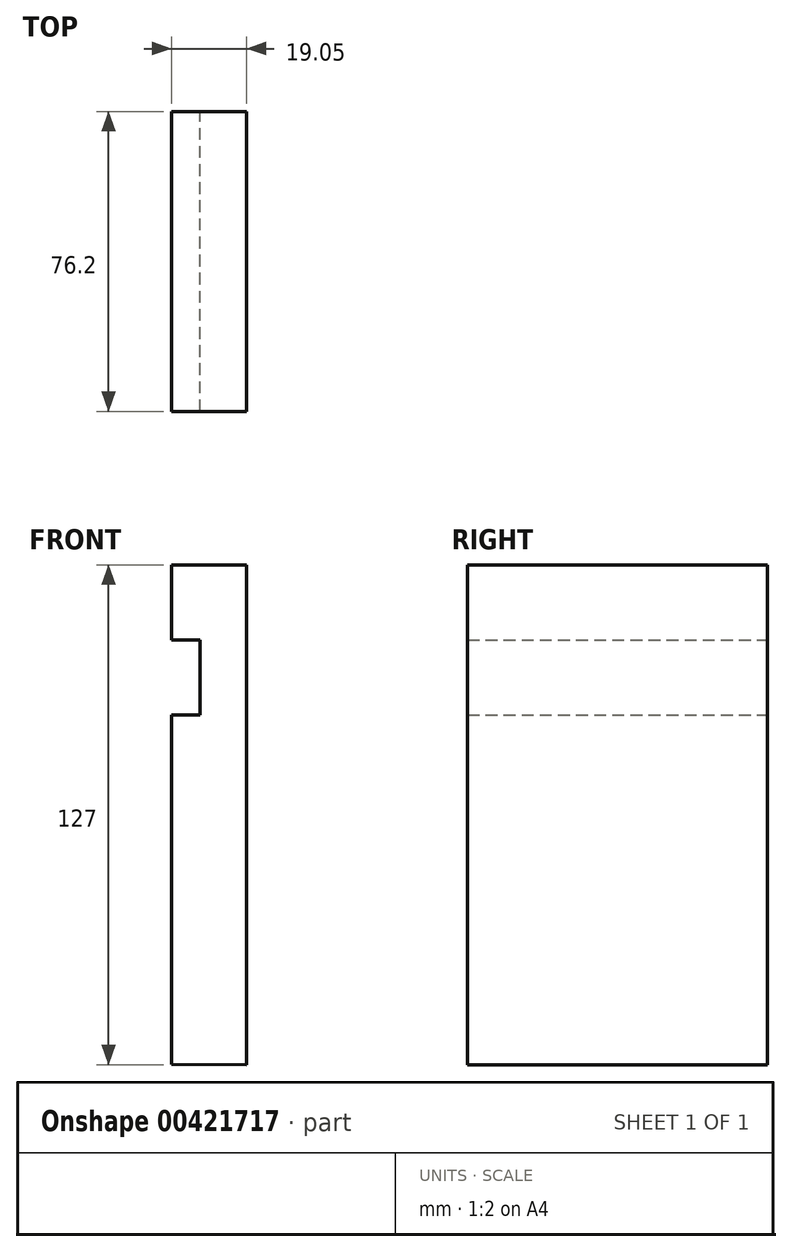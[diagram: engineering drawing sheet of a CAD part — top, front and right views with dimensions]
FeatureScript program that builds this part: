
annotation { "Feature Type Name" : "Feature", "Feature Type Description" : "" }
export const myFeature = defineFeature(function(context is Context, id is Id, definition is map)
    precondition{}
    {
        {
            var Q0;
            Q0=qCreatedBy(makeId("Front.planeOp"),FACE);
            var sketch = newSketch(context, id + "F0", { "sketchPlane" : qUnion([Q0])});
            skLineSegment(sketch, "E0", {"start": v(0, -61.24) * mm, "end": v(0, 65.76) * mm});
            skLineSegment(sketch, "E1", {"start": v(0, 65.76) * mm, "end": v(-19.05, 65.76) * mm});
            skLineSegment(sketch, "E2", {"start": v(-19.05, 65.76) * mm, "end": v(-19.05, 46.7) * mm});
            skLineSegment(sketch, "E3", {"start": v(-19.05, 46.7) * mm, "end": v(-11.78, 46.7) * mm});
            skLineSegment(sketch, "E4", {"start": v(-11.78, 46.7) * mm, "end": v(-11.78, 27.66) * mm});
            skLineSegment(sketch, "E5", {"start": v(-11.78, 27.66) * mm, "end": v(-19.05, 27.66) * mm});
            skLineSegment(sketch, "E6", {"start": v(-19.05, 27.66) * mm, "end": v(-19.05, -61.12) * mm});
            skLineSegment(sketch, "E7", {"start": v(-19.05, -61.12) * mm, "end": v(0, -61.24) * mm});
            skSolve(sketch);
        }
        {
            var Q0;
            Q0=makeQuery(id+"F0.imprint","IMPRINT",FACE,{"disambiguationData":[TD([[makeQuery(id+"F0.imprint","IMPRINT",EDGE,{"derivedFrom":sQuery(id+"F0.wireOp",EDGE,"E0")}),1.0]])]});
            extrude(context, id + "F1", {"entities" : qUnion([Q0]), "depth" : 76.2 * mm});
        }
    });
